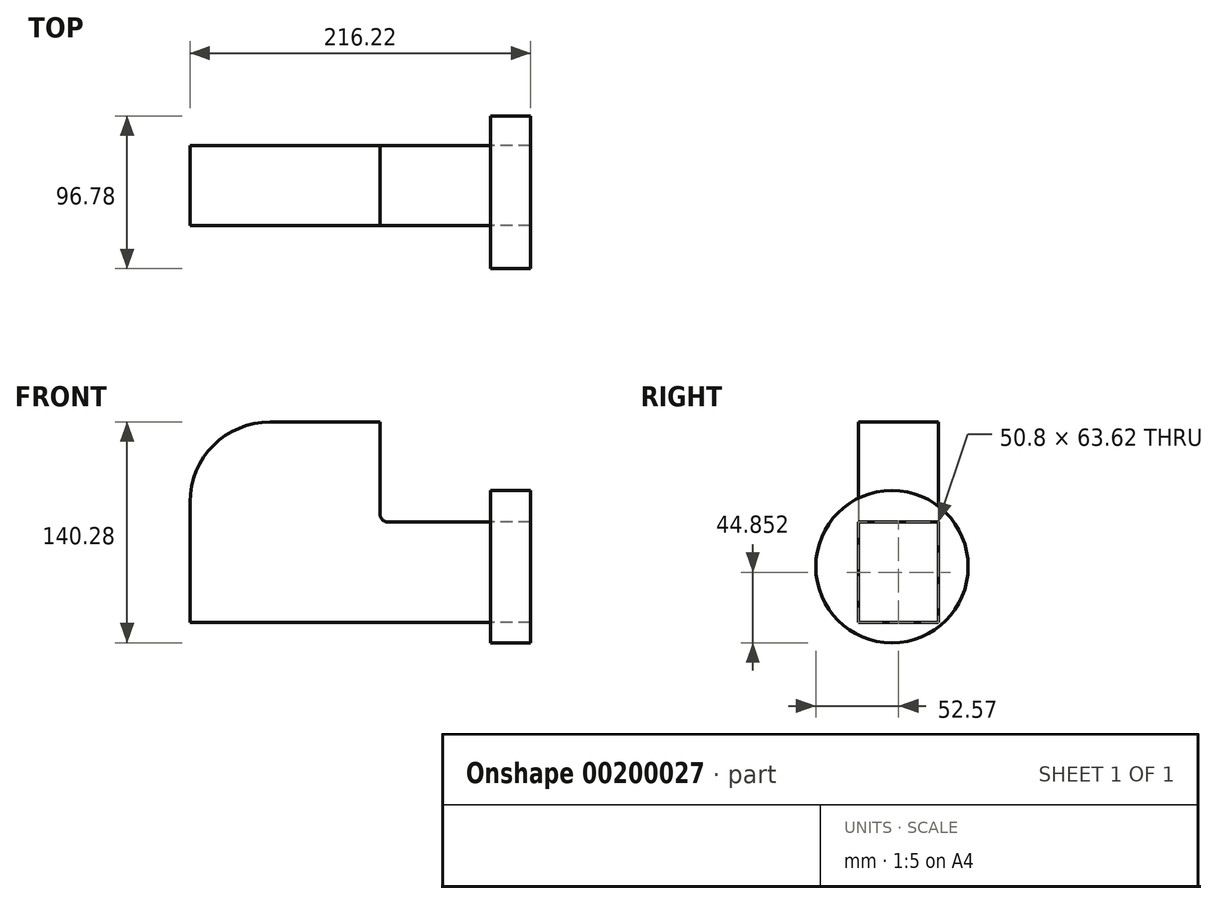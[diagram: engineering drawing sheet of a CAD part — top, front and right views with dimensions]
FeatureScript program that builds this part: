
annotation { "Feature Type Name" : "Feature", "Feature Type Description" : "" }
export const myFeature = defineFeature(function(context is Context, id is Id, definition is map)
    precondition{}
    {
        {
            var Q0;
            Q0=qCreatedBy(makeId("Front.planeOp"),FACE);
            var sketch = newSketch(context, id + "F0", { "sketchPlane" : qUnion([Q0])});
            skLineSegment(sketch, "E0.bottom", {"start": v(-7.5, 100.56) * mm, "end": v(62.34, 100.56) * mm});
            skLineSegment(sketch, "E0.top", {"start": v(-58.3, -26.68) * mm, "end": v(62.34, -26.68) * mm});
            skLineSegment(sketch, "E0.left", {"start": v(-58.3, 49.76) * mm, "end": v(-58.3, -26.68) * mm});
            skLineSegment(sketch, "E0.right", {"start": v(62.34, 100.56) * mm, "end": v(62.34, 36.94) * mm});
            skPoint(sketch, "E1.visualSharp", {"position": v(-58.3, 100.56) * mm});
            skArc(sketch, "E1.filletArc", {"start": v(-7.5, 100.56) * mm, "mid": v(-43.43, 85.68) * mm, "end": v(-58.3, 49.76) * mm});
            skLineSegment(sketch, "E2", {"start": v(62.34, 36.94) * mm, "end": v(132.52, 36.94) * mm});
            skLineSegment(sketch, "E3", {"start": v(132.52, 36.94) * mm, "end": v(132.52, -26.68) * mm});
            skLineSegment(sketch, "E4", {"start": v(132.52, -26.68) * mm, "end": v(62.34, -26.68) * mm});
            skSolve(sketch);
        }
        {
            var Q0;
            Q0=makeQuery(id+"F0.imprint","IMPRINT",FACE,{"disambiguationData":[TD([[makeQuery(id+"F0.imprint","IMPRINT",EDGE,{"derivedFrom":sQuery(id+"F0.wireOp",EDGE,"E0.bottom")}),-1.0]])]});
            extrude(context, id + "F1", {"entities" : qUnion([Q0]), "depth" : 50.8 * mm});
        }
        {
            var Q0;
            Q0=makeQuery(id+"F1.opExtrude","SWEPT_EDGE",EDGE,{"disambiguationData":[OSD([sQuery(id+"F0.wireOp",EDGE,"E0.right"),sQuery(id+"F0.wireOp",EDGE,"E2")])]});
            fillet(context, id + "F2", {"entities" : qUnion([Q0]), "radius" : 5.08 * mm, "tangentPropagation" : true, "allowEdgeOverflow" : false});
        }
        {
            var Q0;
            Q0=makeQuery(id+"F1.opExtrude","SWEPT_FACE",FACE,{"disambiguationData":[OSD([sQuery(id+"F0.wireOp",EDGE,"E3")])]});
            var sketch = newSketch(context, id + "F3", { "sketchPlane" : qUnion([Q0])});
            skCircle(sketch, "E5", {"center": v(-29.58, 8.67) * mm, "radius": 48.39 * mm});
            skSolve(sketch);
        }
        {
            var Q0;
            Q0=makeQuery(id+"F3.imprint","IMPRINT",FACE,{"disambiguationData":[TD([[makeQuery(id+"F3.imprint","IMPRINT",EDGE,{"derivedFrom":sQuery(id+"F3.wireOp",EDGE,"E5")}),1.0]])]});
            extrude(context, id + "F4", {"entities" : qUnion([Q0]), "depth" : 25.4 * mm});
        }
    });
